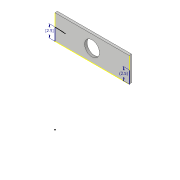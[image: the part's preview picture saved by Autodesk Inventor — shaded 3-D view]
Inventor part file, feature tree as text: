
AUTODESK INVENTOR PART (.ipt)
format: ipt  version: 2019 (Build 230136000, 136)  size: 92,672 bytes
history: native  units: in
note: dims shown in document units (in); Inventor stores cm internally (conversion verified against a paired STEP export)
features: sketch x6, extrude x2
ambient origin geometry x8: Origin, YZ Plane, XZ Plane, XY Plane, X Axis, Y Axis, Z Axis, Center Point
bodies: Solid1 (feature_tree)
feature tree (8):
  sketch  "Sketch1"  dims[d0=5.9055in d1=1.9685in]
  extrude  "Extrusion1"  Depth=1.9685in
  sketch  "Sketch3"  dims[d5=0.9843in]
  sketch  "Sketch4"  dims[d6=2.3622in]
  sketch  "Sketch5"  dims[d7=1.1811in]
  extrude  "Extrusion2"  Depth=0.1969in
  sketch  "Sketch2"  dims[d2=0.1969in d3=0.0in d4=0.9843in]
  sketch  "Sketch6"  dims[d8=2.3622in d9=2.9528in d10=1.1811in d11=0.0in d12=0.0in]
